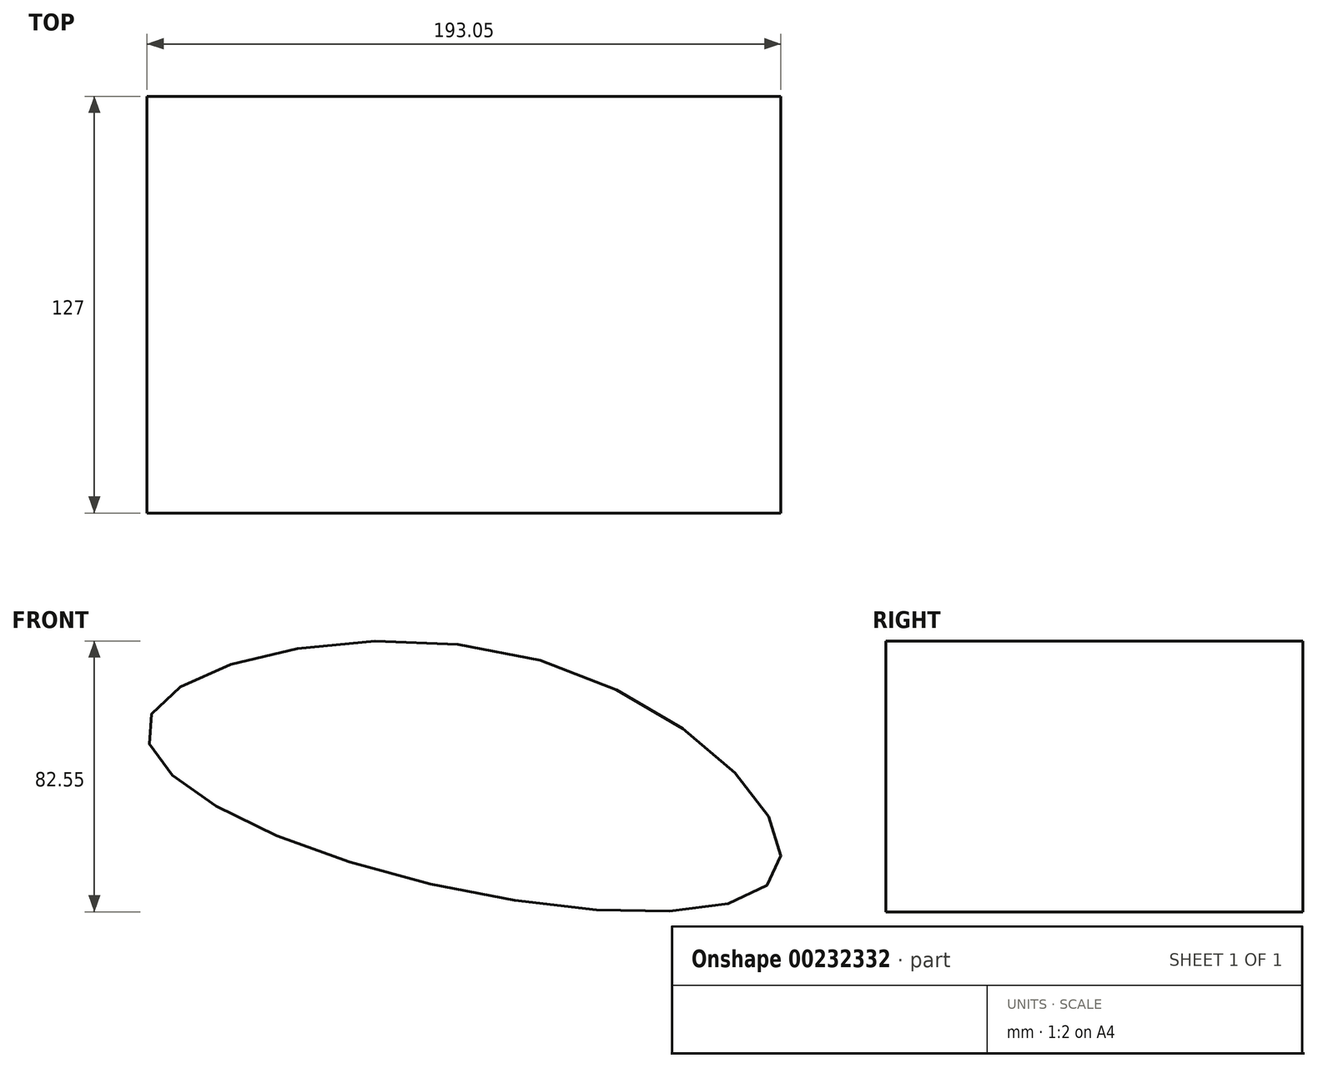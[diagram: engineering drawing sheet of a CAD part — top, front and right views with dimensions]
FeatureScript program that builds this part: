
annotation { "Feature Type Name" : "Feature", "Feature Type Description" : "" }
export const myFeature = defineFeature(function(context is Context, id is Id, definition is map)
    precondition{}
    {
        {
            var Q0;
            Q0=qCreatedBy(makeId("Front.planeOp"),FACE);
            var sketch = newSketch(context, id + "F0", { "sketchPlane" : qUnion([Q0])});
            skFitSpline(sketch, "E0", {"points": [v(-9.78, 3.75) * mm, v(62.37, -61.05) * mm, v(-64.73, -58.64) * mm, v(-128.78, -14.08) * mm, v(-9.78, 3.75) * mm]});
            skSolve(sketch);
        }
        {
            var Q0;
            Q0 = qSketchRegion(id + "F0", true);
            extrude(context, id + "F1", {"entities" : qUnion([Q0]), "depth" : 127 * mm});
        }
    });
